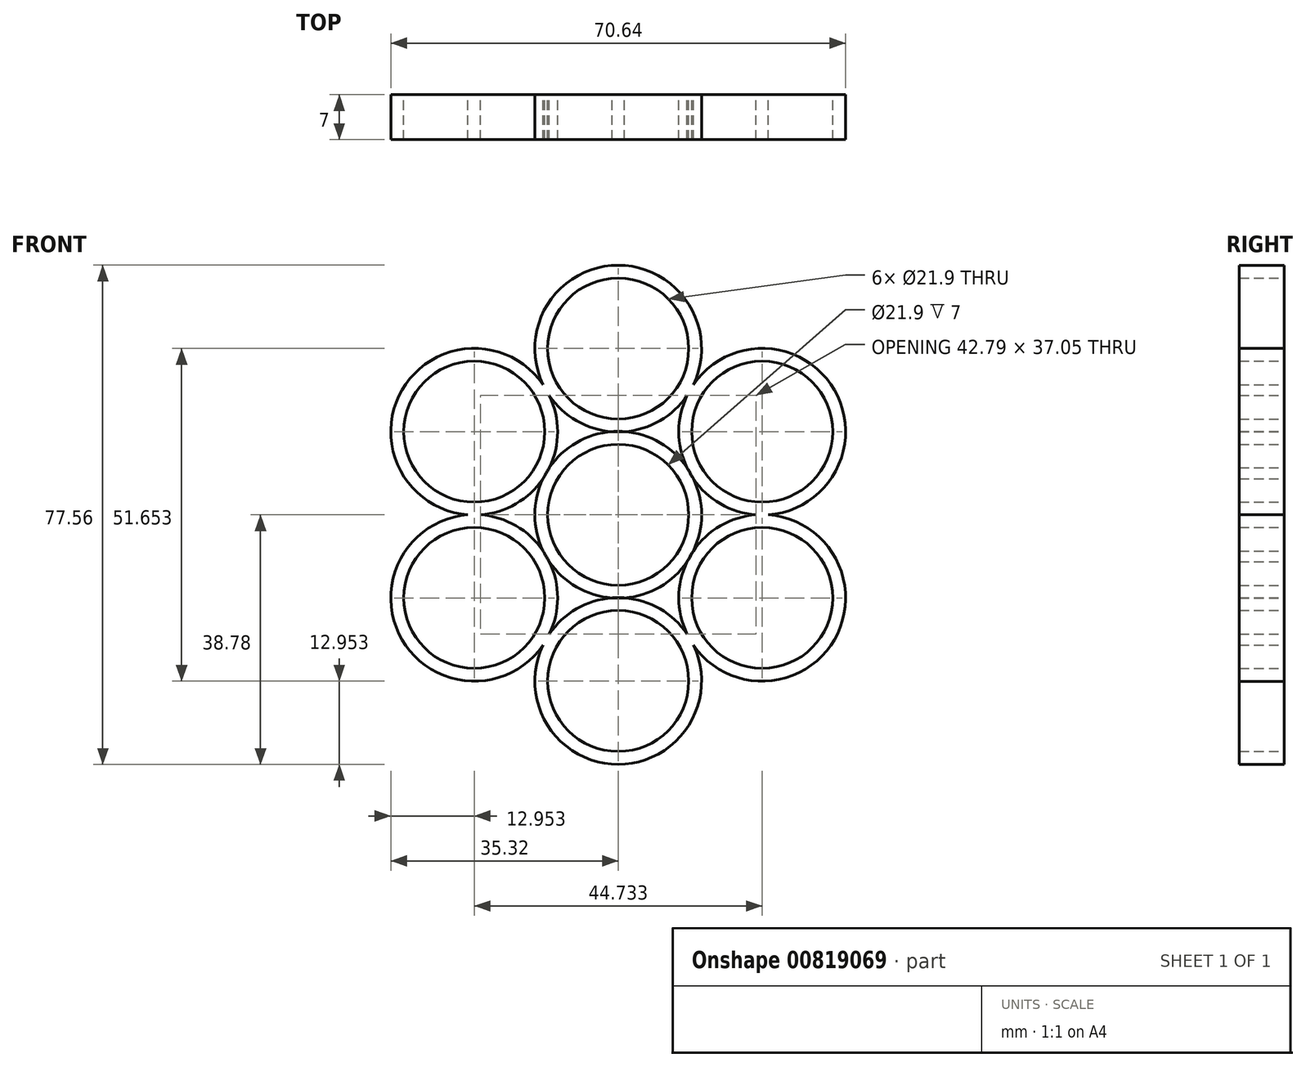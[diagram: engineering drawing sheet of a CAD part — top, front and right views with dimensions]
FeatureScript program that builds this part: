
annotation { "Feature Type Name" : "Feature", "Feature Type Description" : "" }
export const myFeature = defineFeature(function(context is Context, id is Id, definition is map)
    precondition{}
    {
        {
            var Q0;
            Q0=qCreatedBy(makeId("Front.planeOp"),FACE);
            var sketch = newSketch(context, id + "F0", { "sketchPlane" : qUnion([Q0])});
            skCircle(sketch, "E0", {"center": v(0, 0) * mm, "radius": 10.95 * mm});
            skCircle(sketch, "E1.0", {"center": v(0, 0) * mm, "radius": 12.95 * mm});
            skCircle(sketch, "E2", {"center": v(0, 25.83) * mm, "radius": 10.95 * mm});
            skCircle(sketch, "E3.0", {"center": v(0, 25.83) * mm, "radius": 12.95 * mm});
            skCircle(sketch, "E4.1.0", {"center": v(-22.37, 12.91) * mm, "radius": 10.95 * mm});
            skCircle(sketch, "E4.1.1", {"center": v(-22.37, 12.91) * mm, "radius": 12.95 * mm});
            skCircle(sketch, "E4.2.0", {"center": v(-22.37, -12.91) * mm, "radius": 10.95 * mm});
            skCircle(sketch, "E4.2.1", {"center": v(-22.37, -12.91) * mm, "radius": 12.95 * mm});
            skCircle(sketch, "E4.3.0", {"center": v(0, -25.83) * mm, "radius": 10.95 * mm});
            skCircle(sketch, "E4.3.1", {"center": v(0, -25.83) * mm, "radius": 12.95 * mm});
            skCircle(sketch, "E4.4.0", {"center": v(22.37, -12.91) * mm, "radius": 10.95 * mm});
            skCircle(sketch, "E4.4.1", {"center": v(22.37, -12.91) * mm, "radius": 12.95 * mm});
            skCircle(sketch, "E4.5.0", {"center": v(22.37, 12.91) * mm, "radius": 10.95 * mm});
            skCircle(sketch, "E4.5.1", {"center": v(22.37, 12.91) * mm, "radius": 12.95 * mm});
            skSolve(sketch);
        }
        {
            var Q0;
            Q0 = qSketchRegion(id + "F0", true);
            var Q1;
            Q1=makeQuery(id+"F0.imprint","IMPRINT",FACE,{"disambiguationData":[TD([[makeQuery(id+"F0.imprint","IMPRINT",EDGE,{"derivedFrom":sQuery(id+"F0.wireOp",EDGE,"E0")}),-1.0]])]});
            extrude(context, id + "F1", {"entities" : qUnion([Q0, Q1]), "depth" : 7 * mm, "offsetDistance" : 25 * mm});
        }
    });
